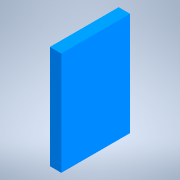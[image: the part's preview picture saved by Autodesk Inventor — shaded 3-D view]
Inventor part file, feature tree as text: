
AUTODESK INVENTOR PART (.ipt)
format: ipt  version: 2022.3 (Build 263350000, 350)  size: 100,864 bytes
history: native  units: in
note: dims shown in document units (in); Inventor stores cm internally (conversion verified against a paired STEP export)
features: extrude x1, sketch x1
ambient origin geometry x8: Origin, YZ Plane, XZ Plane, XY Plane, X Axis, Y Axis, Z Axis, Center Point
bodies: Solid1 (feature_tree)
feature tree (2):
  extrude  "Extrusion1"  Depth=0.5in
  sketch  "Sketch1"  dims[d0=3.0in d1=0.5in d2=4.5in d3=0.0in]
